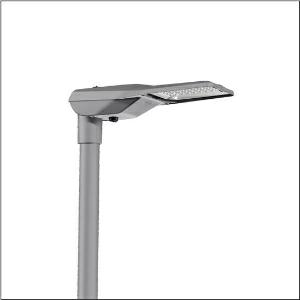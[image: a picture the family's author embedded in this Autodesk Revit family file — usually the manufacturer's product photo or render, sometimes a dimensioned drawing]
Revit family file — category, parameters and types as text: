
# Revit family: streetlight_sl_21_iq_mini___st1_0ab_5xe2m31y08gb_c9fc
name_source: partatom
category: Lighting Fixtures
units: mm (PartAtom-declared; Revit-internal decimal feet)

## family parameters
Cut with Voids When Loaded = No
Host = Face
Light Source = No
Part Type = Normal
Room Calculation Point = No
Round Connector Dimension = Use Diameter
Shared = No

## types (1)
- --- (1 x LED, 5270 lm, 39.8 W, 3000K)
    Apparent Load = 40 VA
    CIE Flux Codes = 38 73 97 100 100
    Color Rendering = 70
    Color Temperature = 3000K
    Default Elevation = 1800 mm
    Description = Streetlight SL 21 iQ mini, mast luminaire, primary light control with lens, of PMMA, primary optical cover: cover, of toughened safety glass, transparent, light distribution: ST1.0aB, light emission: direct distribution, primary light characteristic: asymmetric, installation type: post-top, side-entry, LED, High Power LED, rated luminous flux: 5.270lm, luminous efficacy: 132lm/W, light colour: 730, colour temperature: 3000K, control gear: iQ-Street Remote, D4i with power reduction, control: pre-setting: logarithmic dimming characteristic, Street-Remote, Auto-Match, Temp-Guard, Lumen-Switch, Night-Set, Smart-Wire, Light-Fading, Desk-Remote (wireless, voltage-free reading and setting of iQ features in the workshop via application-optimized NFC function/RFID function), optimised constant luminous flux control (CLO 2.0), mains connection: 220..240V, AC, 50/60Hz, start of lifetime: 40W, end of service life: 41W, reduction: 18W, luminaire housing, of diecast aluminium, powder-coated, SITECO metallic grey (DB 702S), corrosivity category C5 high according to DIN EN ISO 12944, please order mast flange separately, inclination adjustable: 0°, 5°, 10°, 15°, sealing non-destructively replaceable, multi-level sealing system, length: 628mm, width: 235mm, height: 110mm, mast flange for spigot size: 42mm (side-entry): 5XC10008XM4, 60/48mm (side-entry/post-top): 5XC10108XM2, 76/60mm (side-entry/post-top): 5XC10108XM1, mounting height: 4..8m, Smart Interface below and above, protection rating (complete): IP66, insulation class (complete): insulation class II (safety insulation), certification: CE, ENEC, ENEC+, VDE, impact resistance: IK10, permissible operating ambient temperature for outdoor applications: -40..+50°C, standard-compliant lighting for roads and squares, packaging unit: 1 piece

Light Distribution: ST1.0aB
    Height = 110 mm
    Lamp = 1 x LED
    Lamp Light Flux = 5270 lm
    Lamp Power = 39.8 W
    Lamp count = 1
    Length = 625 mm
    Luminous efficacy = 132 lm/W
    Manufacturer = Siteco
    ModVariant = No
    Model = 5XE2M31Y08GB
    Mounting Place = Pole
    Mounting Type = Pole top
    Number of Poles = 1
    OnlyDefault = Yes
    Power Factor = 1
    Product Name = Streetlight SL 21 iQ mini | ST1.0aB
    Product group = mast luminaire | pylon top
    ProductGroupID = 6100
    Protection Class = Protection class II
    Protection Degree = IP 66
    RLX_Detail_Level = 1
    RLX_Emergency_Light_Flux = 0 lm
    RLX_Emergency_Type = 0
    RLX_Emergency_Type_DB = No
    RlxData = <blob elided: 92893 chars, md5=d043c7a1>
    Socket = socket
    Standby Power = 0 W
    System Light Flux = 5270 lm
    System Power = 40 W
    Type Comments = factory setting: luminous flux: 100 % | dim-lin: 254 | 800 mA
    Type Image = l_1003514.jpg
    URL = http://relux.com
    VarID = @adj_113985
    Voltage = 0 V
    Weight = 0.00 kg
    Width = 234 mm

## geometry (parser evidence)
native form markers: Blend x4, Sweep x12
no freeform markers — native parametric forms only
